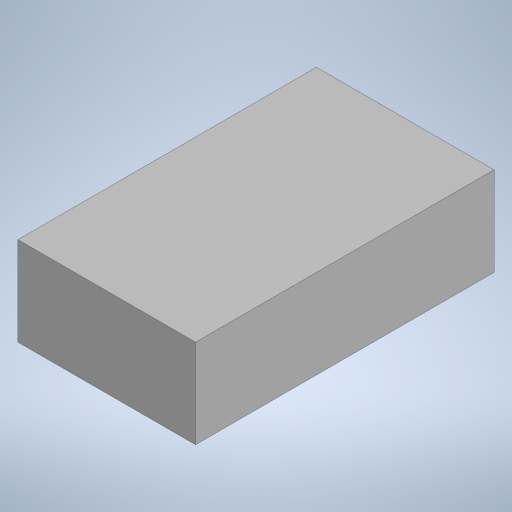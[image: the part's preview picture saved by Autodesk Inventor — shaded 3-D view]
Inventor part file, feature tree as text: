
AUTODESK INVENTOR PART (.ipt)
format: ipt  version: 2023 (Build 270158000, 158)  size: 177,664 bytes
history: native  units: in
note: dims shown in document units (in); Inventor stores cm internally (conversion verified against a paired STEP export)
features: extrude x1, sketch x1
ambient origin geometry x8: Origin, YZ Plane, XZ Plane, XY Plane, X Axis, Y Axis, Z Axis, Center Point
bodies: Solid1 (feature_tree)
feature tree (2):
  extrude  "Extrusion1"  Depth=0.15in TaperAngle=0.0deg
  sketch  "Sketch1"  dims[d0=0.3in d1=0.15in d2=0.0in]
